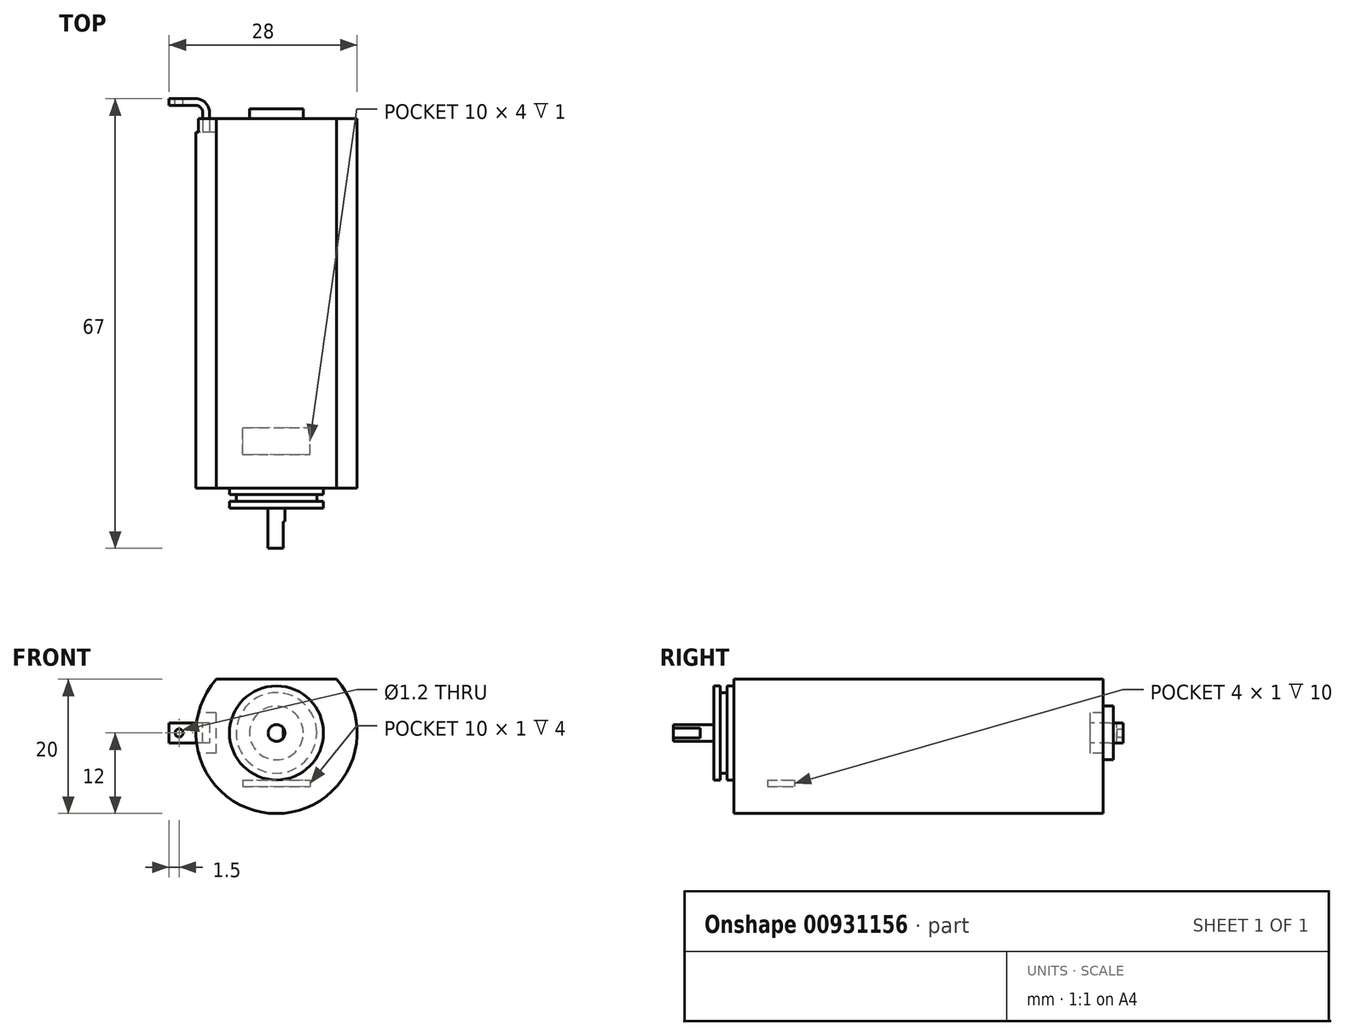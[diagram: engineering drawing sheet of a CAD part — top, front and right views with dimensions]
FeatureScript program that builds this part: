
annotation { "Feature Type Name" : "Feature", "Feature Type Description" : "" }
export const myFeature = defineFeature(function(context is Context, id is Id, definition is map)
    precondition{}
    {
        {
            var Q0;
            Q0=qCreatedBy(makeId("Front.planeOp"),FACE);
            var sketch = newSketch(context, id + "F0", { "sketchPlane" : qUnion([Q0])});
            skCircle(sketch, "E0", {"center": v(0, 0) * mm, "radius": 12 * mm});
            skSolve(sketch);
        }
        {
            var Q0;
            Q0=makeQuery(id+"F0.imprint","IMPRINT",FACE,{"disambiguationData":[TD([[makeQuery(id+"F0.imprint","IMPRINT",EDGE,{"derivedFrom":sQuery(id+"F0.wireOp",EDGE,"E0")}),1.0]])]});
            extrude(context, id + "F1", {"entities" : qUnion([Q0]), "oppositeDirection" : true, "depth" : 55 * mm, "offsetDistance" : 25 * mm});
        }
        {
            var Q0;
            Q0=qCreatedBy(makeId("Front.planeOp"),FACE);
            var sketch = newSketch(context, id + "F2", { "sketchPlane" : qUnion([Q0])});
            skLineSegment(sketch, "E1", {"start": v(0, 19.82) * mm, "end": v(0, -18.22) * mm, "construction": true});
            skLineSegment(sketch, "E2", {"start": v(-25.02, 0) * mm, "end": v(19.88, 0) * mm, "construction": true});
            skLineSegment(sketch, "E3.bottom", {"start": v(-10, 18) * mm, "end": v(10, 18) * mm});
            skLineSegment(sketch, "E3.top", {"start": v(-10, 8) * mm, "end": v(10, 8) * mm});
            skLineSegment(sketch, "E3.left", {"start": v(-10, 18) * mm, "end": v(-10, 8) * mm});
            skLineSegment(sketch, "E3.right", {"start": v(10, 18) * mm, "end": v(10, 8) * mm});
            skSolve(sketch);
        }
        {
            var Q0;
            Q0=makeQuery(id+"F2.imprint","IMPRINT",FACE,{"disambiguationData":[TD([[makeQuery(id+"F2.imprint","IMPRINT",EDGE,{"derivedFrom":sQuery(id+"F2.wireOp",EDGE,"E3.bottom")}),-1.0]])]});
            extrude(context, id + "F3", {"entities" : qUnion([Q0]), "operationType" : NewBodyOperationType.REMOVE, "endBound" : BoundingType.THROUGH_ALL, "oppositeDirection" : true, "depth" : 25 * mm, "offsetDistance" : 25 * mm});
        }
        {
            var Q0;
            Q0=qCreatedBy(makeId("Front.planeOp"),FACE);
            var sketch = newSketch(context, id + "F4", { "sketchPlane" : qUnion([Q0])});
            skCircle(sketch, "E4", {"center": v(0, 0) * mm, "radius": 7 * mm});
            skSolve(sketch);
        }
        {
            var Q0;
            Q0=makeQuery(id+"F4.imprint","IMPRINT",FACE,{"disambiguationData":[TD([[makeQuery(id+"F4.imprint","IMPRINT",EDGE,{"derivedFrom":sQuery(id+"F4.wireOp",EDGE,"E4")}),1.0]])]});
            extrude(context, id + "F5", {"entities" : qUnion([Q0]), "operationType" : NewBodyOperationType.ADD, "depth" : 3 * mm, "offsetDistance" : 25 * mm});
        }
        {
            var Q0;
            Q0=qCreatedBy(makeId("Front.planeOp"),FACE);
            var sketch = newSketch(context, id + "F6", { "sketchPlane" : qUnion([Q0])});
            skCircle(sketch, "E5", {"center": v(0, 0) * mm, "radius": 1.25 * mm});
            skSolve(sketch);
        }
        {
            var Q0;
            Q0 = qSketchRegion(id + "F6", true);
            extrude(context, id + "F7", {"entities" : qUnion([Q0]), "operationType" : NewBodyOperationType.ADD, "depth" : 9 * mm, "offsetDistance" : 25 * mm});
        }
        {
            var Q0;
            Q0=qCreatedBy(makeId("Right.planeOp"),FACE);
            var sketch = newSketch(context, id + "F8", { "sketchPlane" : qUnion([Q0])});
            skLineSegment(sketch, "E6", {"start": v(0, -2.24) * mm, "end": v(0, 11.87) * mm, "construction": true});
            skLineSegment(sketch, "E7", {"start": v(1.62, 0) * mm, "end": v(-11.64, 0) * mm, "construction": true});
            skLineSegment(sketch, "E8.bottom", {"start": v(-2, 7) * mm, "end": v(-1, 7) * mm});
            skLineSegment(sketch, "E8.top", {"start": v(-2, 6) * mm, "end": v(-1, 6) * mm});
            skLineSegment(sketch, "E8.left", {"start": v(-2, 7) * mm, "end": v(-2, 6) * mm});
            skLineSegment(sketch, "E8.right", {"start": v(-1, 7) * mm, "end": v(-1, 6) * mm});
            skLineSegment(sketch, "E9", {"start": v(-3, 7) * mm, "end": v(0, 7) * mm, "construction": true});
            skSolve(sketch);
        }
        {
            var Q0;
            Q0 = qSketchRegion(id + "F8", true);
            var Q1;
            Q1=sQuery(id+"F8.wireOp",EDGE,"E7");
            revolve(context, id + "F9", {"operationType" : NewBodyOperationType.REMOVE, "surfaceOperationType" : NewSurfaceOperationType.NEW, "entities" : qUnion([Q0]), "axis" : qUnion([Q1]), "revolveType" : RevolveType.FULL, "oppositeDirection" : true});
        }
        {
            var Q0;
            Q0=qCreatedBy(makeId("Front.planeOp"),FACE);
            cPlane(context, id + "F10", {"entities" : qUnion([Q0]), "cplaneType" : CPlaneType.OFFSET, "offset" : 9 * mm, "width" : 150 * mm, "height" : 150 * mm});
        }
        {
            var Q0;
            Q0=qCreatedBy(id+"F10.planeOp",FACE);
            var sketch = newSketch(context, id + "F11", { "sketchPlane" : qUnion([Q0])});
            skLineSegment(sketch, "E10", {"start": v(0, 3.43) * mm, "end": v(0, -4.16) * mm, "construction": true});
            skLineSegment(sketch, "E11", {"start": v(-4.09, 0) * mm, "end": v(6, 0) * mm, "construction": true});
            skLineSegment(sketch, "E12.bottom", {"start": v(1, 2.5) * mm, "end": v(4, 2.5) * mm});
            skLineSegment(sketch, "E12.top", {"start": v(1, -2.5) * mm, "end": v(4, -2.5) * mm});
            skLineSegment(sketch, "E12.left", {"start": v(1, 2.5) * mm, "end": v(1, -2.5) * mm});
            skLineSegment(sketch, "E12.right", {"start": v(4, 2.5) * mm, "end": v(4, -2.5) * mm});
            skSolve(sketch);
        }
        {
            var Q0;
            Q0=makeQuery(id+"F11.imprint","IMPRINT",FACE,{"disambiguationData":[TD([[makeQuery(id+"F11.imprint","IMPRINT",EDGE,{"derivedFrom":sQuery(id+"F11.wireOp",EDGE,"E12.bottom")}),-1.0]])]});
            extrude(context, id + "F12", {"entities" : qUnion([Q0]), "operationType" : NewBodyOperationType.REMOVE, "oppositeDirection" : true, "depth" : 4 * mm, "offsetDistance" : 25 * mm});
        }
        {
            var Q0;
            Q0=qCreatedBy(makeId("Top.planeOp"),FACE);
            cPlane(context, id + "F13", {"entities" : qUnion([Q0]), "cplaneType" : CPlaneType.OFFSET, "offset" : 8 * mm, "oppositeDirection" : true, "width" : 150 * mm, "height" : 150 * mm});
        }
        {
            var Q0;
            Q0=qCreatedBy(id+"F13.planeOp",FACE);
            var sketch = newSketch(context, id + "F14", { "sketchPlane" : qUnion([Q0])});
            skLineSegment(sketch, "E13", {"start": v(0, -16.46) * mm, "end": v(0, 26.87) * mm, "construction": true});
            skLineSegment(sketch, "E14", {"start": v(-24.85, 0) * mm, "end": v(23.34, 0) * mm, "construction": true});
            skLineSegment(sketch, "E15.bottom", {"start": v(-5, 5) * mm, "end": v(5, 5) * mm});
            skLineSegment(sketch, "E15.top", {"start": v(-5, 9) * mm, "end": v(5, 9) * mm});
            skLineSegment(sketch, "E15.left", {"start": v(-5, 5) * mm, "end": v(-5, 9) * mm});
            skLineSegment(sketch, "E15.right", {"start": v(5, 5) * mm, "end": v(5, 9) * mm});
            skSolve(sketch);
        }
        {
            var Q0;
            Q0 = qSketchRegion(id + "F14", true);
            extrude(context, id + "F15", {"entities" : qUnion([Q0]), "operationType" : NewBodyOperationType.REMOVE, "depth" : 1 * mm, "offsetDistance" : 25 * mm});
        }
        {
            var Q0;
            Q0=qCreatedBy(makeId("Front.planeOp"),FACE);
            cPlane(context, id + "F16", {"entities" : qUnion([Q0]), "cplaneType" : CPlaneType.OFFSET, "offset" : 55 * mm, "oppositeDirection" : true, "width" : 150 * mm, "height" : 150 * mm});
        }
        {
            var Q0;
            Q0=qCreatedBy(id+"F16.planeOp",FACE);
            var sketch = newSketch(context, id + "F17", { "sketchPlane" : qUnion([Q0])});
            skCircle(sketch, "E16", {"center": v(0, 0) * mm, "radius": 4 * mm});
            skSolve(sketch);
        }
        {
            var Q0;
            Q0=makeQuery(id+"F17.imprint","IMPRINT",FACE,{"disambiguationData":[TD([[makeQuery(id+"F17.imprint","IMPRINT",EDGE,{"derivedFrom":sQuery(id+"F17.wireOp",EDGE,"E16")}),1.0]])]});
            extrude(context, id + "F18", {"entities" : qUnion([Q0]), "operationType" : NewBodyOperationType.ADD, "oppositeDirection" : true, "depth" : 1.5 * mm, "offsetDistance" : 25 * mm});
        }
        {
            var Q0;
            Q0=qCreatedBy(makeId("Front.planeOp"),FACE);
            cPlane(context, id + "F19", {"entities" : qUnion([Q0]), "cplaneType" : CPlaneType.OFFSET, "offset" : 53 * mm, "oppositeDirection" : true, "width" : 150 * mm, "height" : 150 * mm});
        }
        {
            var Q0;
            Q0=qCreatedBy(id+"F19.planeOp",FACE);
            var sketch = newSketch(context, id + "F20", { "sketchPlane" : qUnion([Q0])});
            skLineSegment(sketch, "E17", {"start": v(19.12, 0) * mm, "end": v(-18.63, 0) * mm, "construction": true});
            skLineSegment(sketch, "E18", {"start": v(0, 18.5) * mm, "end": v(0, -15.66) * mm, "construction": true});
            skLineSegment(sketch, "E19.bottom", {"start": v(-9, 3) * mm, "end": v(-15, 3) * mm});
            skLineSegment(sketch, "E19.top", {"start": v(-9, -3) * mm, "end": v(-15, -3) * mm});
            skLineSegment(sketch, "E19.left", {"start": v(-9, 3) * mm, "end": v(-9, -3) * mm});
            skLineSegment(sketch, "E19.right", {"start": v(-15, 3) * mm, "end": v(-15, -3) * mm});
            skSolve(sketch);
        }
        {
            var Q0;
            Q0=makeQuery(id+"F20.imprint","IMPRINT",FACE,{"disambiguationData":[TD([[makeQuery(id+"F20.imprint","IMPRINT",EDGE,{"derivedFrom":sQuery(id+"F20.wireOp",EDGE,"E19.bottom")}),1.0]])]});
            extrude(context, id + "F21", {"entities" : qUnion([Q0]), "operationType" : NewBodyOperationType.REMOVE, "oppositeDirection" : true, "depth" : 25 * mm, "offsetDistance" : 25 * mm});
        }
        {
            var Q0;
            Q0=qCreatedBy(id+"F19.planeOp",FACE);
            var sketch = newSketch(context, id + "F22", { "sketchPlane" : qUnion([Q0])});
            skLineSegment(sketch, "E20", {"start": v(3.67, 0) * mm, "end": v(-12.36, 0) * mm, "construction": true});
            skLineSegment(sketch, "E21", {"start": v(0, -4.3) * mm, "end": v(0, 2.87) * mm, "construction": true});
            skLineSegment(sketch, "E22.bottom", {"start": v(-10, 1.5) * mm, "end": v(-16, 1.5) * mm});
            skLineSegment(sketch, "E22.top", {"start": v(-10, -1.5) * mm, "end": v(-16, -1.5) * mm});
            skLineSegment(sketch, "E22.left", {"start": v(-10, 1.5) * mm, "end": v(-10, -1.5) * mm});
            skLineSegment(sketch, "E22.right", {"start": v(-16, 1.5) * mm, "end": v(-16, -1.5) * mm});
            skSolve(sketch);
        }
        {
            var Q0;
            Q0=makeQuery(id+"F22.imprint","IMPRINT",FACE,{"disambiguationData":[TD([[makeQuery(id+"F22.imprint","IMPRINT",EDGE,{"derivedFrom":sQuery(id+"F22.wireOp",EDGE,"E22.bottom")}),1.0]])]});
            extrude(context, id + "F23", {"entities" : qUnion([Q0]), "operationType" : NewBodyOperationType.ADD, "oppositeDirection" : true, "depth" : 5 * mm, "offsetDistance" : 25 * mm});
        }
        {
            var Q0;
            Q0=makeQuery(id+"F23.opExtrude","CAP_EDGE",EDGE,{"disambiguationData":[OSD([sQuery(id+"F22.wireOp",EDGE,"E22.left")])],"isStart":false});
            fillet(context, id + "F24", {"entities" : qUnion([Q0]), "radius" : 2 * mm, "tangentPropagation" : true, "allowEdgeOverflow" : false});
        }
        {
            var Q0;
            Q0=qCreatedBy(makeId("Top.planeOp"),FACE);
            var sketch = newSketch(context, id + "F25", { "sketchPlane" : qUnion([Q0])});
            skLineSegment(sketch, "E23.0", {"start": v(-12, 57) * mm, "end": v(-16, 57) * mm});
            skArc(sketch, "E23.1", {"start": v(-11, 56) * mm, "mid": v(-11.3, 56.7) * mm, "end": v(-12, 57) * mm});
            skLineSegment(sketch, "E23.2", {"start": v(-11, 56) * mm, "end": v(-11, 53) * mm});
            skLineSegment(sketch, "E24.0", {"start": v(-16, 57) * mm, "end": v(-16, 53) * mm});
            skPoint(sketch, "E25.orphan", {"position": v(-16, 58) * mm});
            skLineSegment(sketch, "E26.0", {"start": v(-11.9, 53) * mm, "end": v(-16, 53) * mm});
            skLineSegment(sketch, "E27.0", {"start": v(-11, 53) * mm, "end": v(-11.9, 53) * mm});
            skPoint(sketch, "E28.orphan", {"position": v(-10, 53) * mm});
            skSolve(sketch);
        }
        {
            var Q0;
            Q0 = qSketchRegion(id + "F25", true);
            extrude(context, id + "F26", {"entities" : qUnion([Q0]), "operationType" : NewBodyOperationType.REMOVE, "endBound" : BoundingType.SYMMETRIC, "oppositeDirection" : true, "depth" : 3 * mm, "offsetDistance" : 25 * mm});
        }
        {
            var Q0;
            Q0=qCreatedBy(id+"F19.planeOp",FACE);
            cPlane(context, id + "F27", {"entities" : qUnion([Q0]), "cplaneType" : CPlaneType.OFFSET, "offset" : 5 * mm, "oppositeDirection" : true, "width" : 150 * mm, "height" : 150 * mm});
        }
        {
            var Q0;
            Q0=qCreatedBy(id+"F27.planeOp",FACE);
            var sketch = newSketch(context, id + "F28", { "sketchPlane" : qUnion([Q0])});
            skLineSegment(sketch, "E29", {"start": v(0.54, 0) * mm, "end": v(-3.65, 0) * mm, "construction": true});
            skLineSegment(sketch, "E30", {"start": v(0, -1.37) * mm, "end": v(0, 0.31) * mm, "construction": true});
            skCircle(sketch, "E31", {"center": v(-14.5, 0) * mm, "radius": 0.6 * mm});
            skSolve(sketch);
        }
        {
            var Q0;
            Q0=makeQuery(id+"F28.imprint","IMPRINT",FACE,{"disambiguationData":[TD([[makeQuery(id+"F28.imprint","IMPRINT",EDGE,{"derivedFrom":sQuery(id+"F28.wireOp",EDGE,"E31")}),1.0]])]});
            extrude(context, id + "F29", {"entities" : qUnion([Q0]), "operationType" : NewBodyOperationType.REMOVE, "endBound" : BoundingType.UP_TO_NEXT, "depth" : 25 * mm, "offsetDistance" : 25 * mm});
        }
    });
